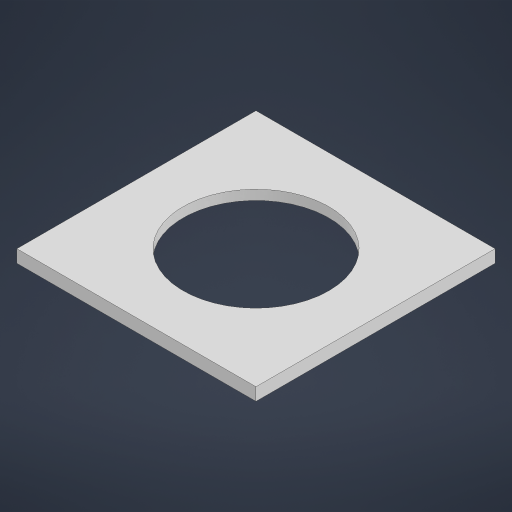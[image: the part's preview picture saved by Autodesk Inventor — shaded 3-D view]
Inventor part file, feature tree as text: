
AUTODESK INVENTOR PART (.ipt)
format: ipt  version: 2024.1 (Build 281209000, 209)  size: 443,904 bytes
history: native  units: mm
features: extrude x2, sketch x2, projected_geometry x1
ambient origin geometry x8: Origin, YZ Plane, XZ Plane, XY Plane, X Axis, Y Axis, Z Axis, Center Point
bodies: Solid1 (feature_tree)
feature tree (5):
  extrude  "Extrusion1"  Depth=18.6mm
  extrude  "Extrusion2"  Depth=0.3mm TaperAngle=0.0deg
  sketch  "Sketch1"  dims[d0=18.6mm d1=18.6mm]
  sketch  "Sketch2"  dims[d2=3.0mm d3=0.3mm d4=0.0mm d5=15.0mm d6=1.0mm d7=0.0mm]
  projected_geometry  "Projected Loop1"
